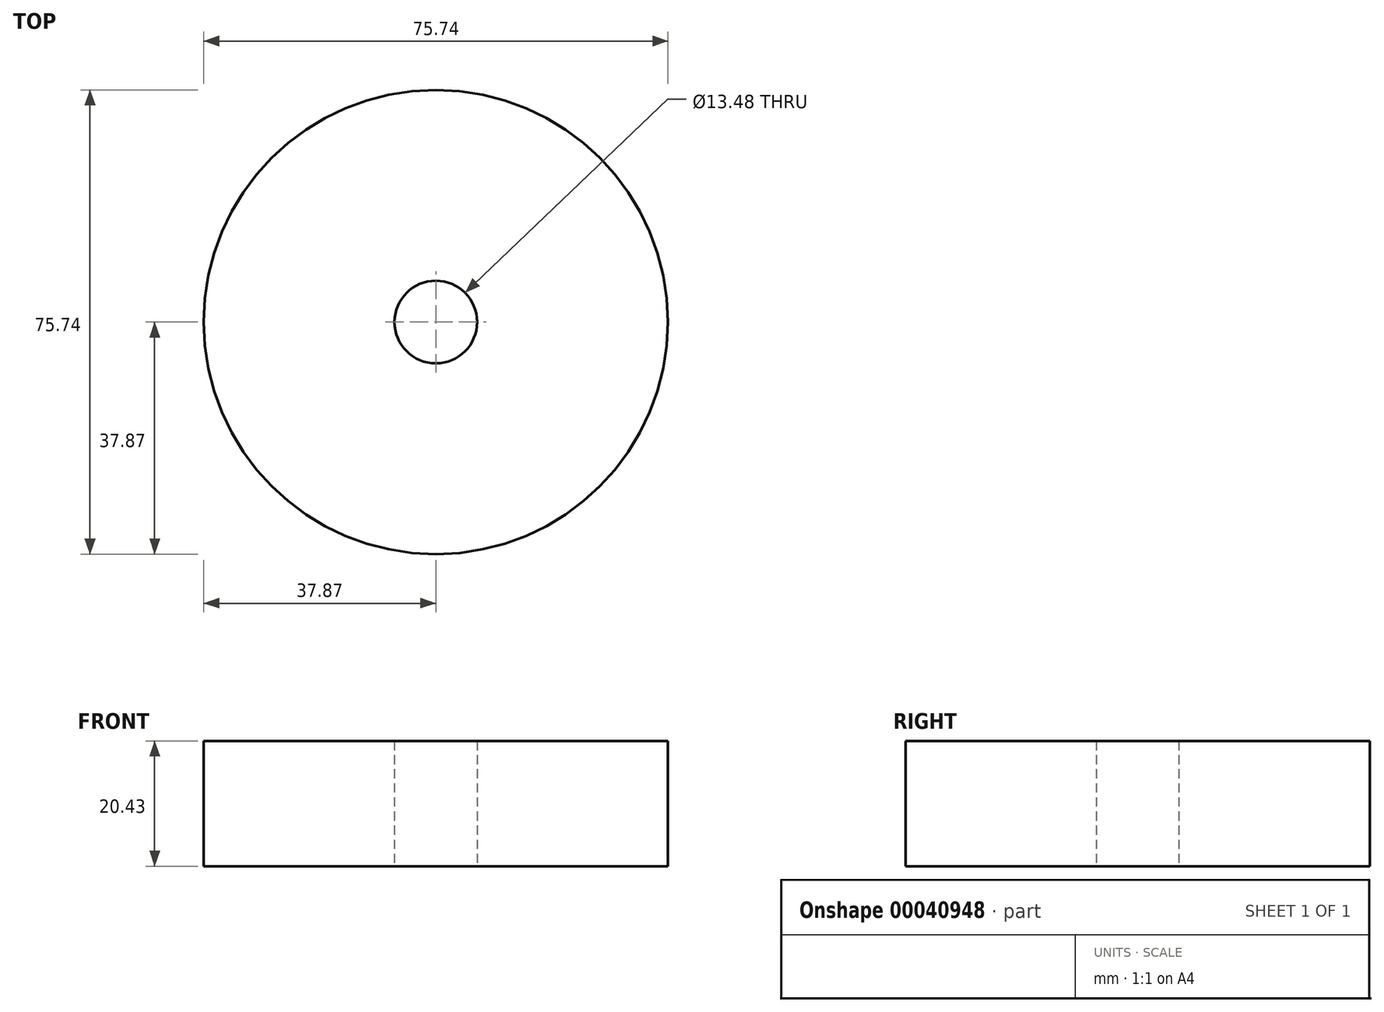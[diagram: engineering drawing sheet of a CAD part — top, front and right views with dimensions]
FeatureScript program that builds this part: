
annotation { "Feature Type Name" : "Feature", "Feature Type Description" : "" }
export const myFeature = defineFeature(function(context is Context, id is Id, definition is map)
    precondition{}
    {
        {
            var Q0;
            Q0=qCreatedBy(makeId("Front.planeOp"),FACE);
            var sketch = newSketch(context, id + "F0", { "sketchPlane" : qUnion([Q0])});
            skFitSpline(sketch, "E0.0", {"points": [v(26.97, 35.2) * mm, v(27.7, 34.54) * mm, v(28.87, 33.54) * mm, v(30.27, 32.09) * mm, v(31, 31.14) * mm, v(31.44, 30.34) * mm, v(31.7, 29.73) * mm, v(31.9, 29.1) * mm, v(32.05, 28.18) * mm, v(32.08, 26.92) * mm, v(31.87, 25.25) * mm, v(31.45, 23.47) * mm, v(30.86, 21.6) * mm, v(30.15, 19.68) * mm, v(29.37, 17.75) * mm, v(28.56, 15.8) * mm, v(27.49, 13.14) * mm, v(26.5, 10.4) * mm, v(25.76, 7.5) * mm, v(25.37, 5.24) * mm, v(25.2, 2.88) * mm, v(25.23, 0.48) * mm, v(25.45, -1.94) * mm, v(25.95, -5.16) * mm, v(26.73, -8.31) * mm, v(27.71, -11.27) * mm, v(28.52, -13.37) * mm, v(29.38, -15.3) * mm, v(30.27, -17.11) * mm, v(31.15, -18.85) * mm, v(32, -20.56) * mm, v(32.8, -22.29) * mm, v(33.42, -23.8) * mm, v(33.87, -25.06) * mm, v(34.29, -26.38) * mm, v(34.73, -28.1) * mm, v(35.08, -30.17) * mm, v(35.2, -32.12) * mm, v(35.07, -33.54) * mm, v(34.82, -34.48) * mm, v(34.57, -35.08) * mm, v(34.26, -35.55) * mm, v(33.9, -35.91) * mm, v(33.42, -36.21) * mm, v(32.83, -36.45) * mm, v(32.13, -36.61) * mm, v(31.05, -36.73) * mm, v(29.48, -36.7) * mm, v(27.37, -36.43) * mm, v(25.14, -35.98) * mm, v(23.26, -35.51) * mm, v(21.8, -35.12) * mm, v(20.36, -34.74) * mm, v(18.63, -34.27) * mm, v(16.65, -33.74) * mm, v(14.73, -33.29) * mm, v(12.88, -32.93) * mm, v(11.38, -32.74) * mm, v(10.2, -32.67) * mm, v(9.03, -32.65) * mm, v(7.6, -32.75) * mm, v(5.93, -33) * mm, v(4.26, -33.31) * mm, v(2.83, -33.6) * mm, v(1.65, -33.83) * mm, v(0.74, -34) * mm, v(-0.2, -34.15) * mm, v(-1.5, -34.32) * mm, v(-3.14, -34.44) * mm, v(-4.67, -34.3) * mm, v(-5.75, -33.97) * mm, v(-6.48, -33.61) * mm, v(-7.13, -33.12) * mm, v(-7.7, -32.47) * mm, v(-8.21, -31.6) * mm, v(-8.77, -30.13) * mm, v(-9, -28.59) * mm, v(-9.04, -27.34) * mm]});
            skLineSegment(sketch, "E1", {"start": v(0, 0) * mm, "end": v(0, 49.9) * mm, "construction": true});
            skFitSpline(sketch, "E2.0", {"points": [v(28.68, 37.08) * mm, v(29.02, 36.77) * mm, v(29.76, 36.11) * mm, v(30.98, 35.01) * mm, v(32.19, 33.76) * mm, v(33.1, 32.56) * mm, v(33.64, 31.62) * mm, v(33.9, 31.04) * mm, v(34.08, 30.6) * mm, v(34.24, 30.13) * mm, v(34.4, 29.5) * mm, v(34.54, 28.7) * mm, v(34.6, 27.74) * mm, v(34.58, 26.43) * mm, v(34.37, 24.78) * mm, v(33.9, 22.78) * mm, v(33.26, 20.77) * mm, v(32.52, 18.76) * mm, v(31.72, 16.78) * mm, v(30.9, 14.82) * mm, v(29.86, 12.23) * mm, v(28.92, 9.62) * mm, v(28.33, 7.3) * mm, v(28.07, 5.94) * mm, v(27.92, 4.91) * mm, v(27.82, 3.87) * mm, v(27.74, 2.45) * mm, v(27.77, 0.62) * mm, v(27.97, -1.63) * mm, v(28.32, -3.89) * mm, v(28.81, -6.13) * mm, v(29.41, -8.32) * mm, v(30.1, -10.42) * mm, v(30.74, -12.06) * mm, v(31.27, -13.3) * mm, v(31.82, -14.51) * mm, v(32.82, -16.55) * mm, v(34, -18.84) * mm, v(35.13, -21.27) * mm, v(35.8, -22.88) * mm, v(36.28, -24.25) * mm, v(36.73, -25.68) * mm, v(37.22, -27.56) * mm, v(37.6, -29.86) * mm, v(37.75, -32.13) * mm, v(37.6, -33.93) * mm, v(37.24, -35.29) * mm, v(36.9, -36.1) * mm, v(36.54, -36.7) * mm, v(36.23, -37.14) * mm, v(35.86, -37.54) * mm, v(35.31, -38.03) * mm, v(34.56, -38.5) * mm, v(33.57, -38.88) * mm, v(32.55, -39.12) * mm, v(31.12, -39.28) * mm, v(29.27, -39.24) * mm, v(26.94, -38.93) * mm, v(24.57, -38.45) * mm, v(22.24, -37.87) * mm, v(20.04, -37.28) * mm, v(17.97, -36.72) * mm, v(16.02, -36.2) * mm, v(14.19, -35.77) * mm, v(12.47, -35.44) * mm, v(10.86, -35.23) * mm, v(9.6, -35.19) * mm, v(8.62, -35.23) * mm, v(7.63, -35.32) * mm, v(6.36, -35.5) * mm, v(4.76, -35.8) * mm, v(3.05, -36.15) * mm, v(1.5, -36.45) * mm, v(0.17, -36.66) * mm, v(-0.88, -36.8) * mm, v(-1.99, -36.9) * mm, v(-3.52, -36.96) * mm, v(-5.1, -36.82) * mm, v(-6.67, -36.35) * mm, v(-7.8, -35.8) * mm, v(-8.87, -35) * mm, v(-9.79, -33.96) * mm, v(-10.53, -32.68) * mm, v(-11.27, -30.67) * mm, v(-11.53, -28.83) * mm, v(-11.57, -27.41) * mm]});
            skLineSegment(sketch, "E3", {"start": v(29.06, 36.73) * mm, "end": v(27.34, 34.87) * mm});
            skLineSegment(sketch, "E4", {"start": v(1.12, -36.5) * mm, "end": v(0.74, -34) * mm});
            skSolve(sketch);
        }
        {
            var Q0;
            Q0=qCreatedBy(makeId("Front.planeOp"),FACE);
            var sketch = newSketch(context, id + "F1", { "sketchPlane" : qUnion([Q0])});
            skLineSegment(sketch, "E5.bottom", {"start": v(-6.74, -7.63) * mm, "end": v(-37.87, -7.63) * mm});
            skLineSegment(sketch, "E5.top", {"start": v(-6.74, -28.06) * mm, "end": v(-37.87, -28.06) * mm});
            skLineSegment(sketch, "E5.left", {"start": v(-6.74, -7.63) * mm, "end": v(-6.74, -28.06) * mm});
            skLineSegment(sketch, "E5.right", {"start": v(-37.87, -7.63) * mm, "end": v(-37.87, -28.06) * mm});
            skSolve(sketch);
        }
        {
            var Q0;
            Q0=makeQuery(id+"F1.imprint","IMPRINT",FACE,{"disambiguationData":[TD([[makeQuery(id+"F1.imprint","IMPRINT",EDGE,{"derivedFrom":sQuery(id+"F1.wireOp",EDGE,"E5.bottom")}),1.0]])]});
            var Q1;
            Q1=sQuery(id+"F0.wireOp",EDGE,"E1");
            revolve(context, id + "F2", {"entities" : qUnion([Q0]), "axis" : qUnion([Q1]), "revolveType" : RevolveType.FULL});
        }
    });
